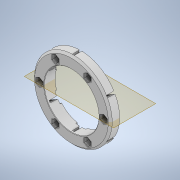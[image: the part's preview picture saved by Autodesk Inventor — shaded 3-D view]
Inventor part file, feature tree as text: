
AUTODESK INVENTOR PART (.ipt)
format: ipt  version: 2020 (Build 240168000, 168)  size: 5,638,656 bytes
history: native  units: in
note: dims shown in document units (in); Inventor stores cm internally (conversion verified against a paired STEP export)
features: extrude x7, sketch x7, other x4, chamfer x2, pattern_circular x2, reference x2, imported_body x1, boolean_combine x1, plane x1, fillet x1, projected_geometry x1
ambient origin geometry x8: Origin, YZ Plane, XZ Plane, XY Plane, X Axis, Y Axis, Z Axis, Center Point
bodies: Solid1 (feature_tree), Solid2 (feature_tree)
feature tree (29):
  extrude  "Extrusion1"  Depth=0.7in TaperAngle=0.0deg
  extrude  "Extrusion2"  Depth=2.3622in TaperAngle=360.0deg
  imported_body  "Base1"
  boolean_combine  "Combine1"
  extrude  "Extrusion3"  Depth=0.4375in
  extrude  "Extrusion4"  Depth=0.3in TaperAngle=0.0deg
  extrude  "Extrusion5"  Depth=0.0118in TaperAngle=0.0deg
  chamfer  "Chamfer1"  Distance=2.3622in Angle=360.0deg
  chamfer  "Chamfer2"  Distance=0.0118in
  plane  "Work Plane3"
  extrude  "Extrusion6"  Depth=0.025in TaperAngle=45.0deg
  pattern_circular  "Circular Pattern1"  [2 undecoded]
  extrude  "Extrusion7"  Depth=0.05in TaperAngle=0.0deg
  pattern_circular  "Circular Pattern2"  Count=6 Angle=360.0deg
  fillet  "Fillet1"  Radius=0.0118in
  sketch  "Sketch1"  dims[d0=3.5in d2=0.7in d3=0.0in]
  reference  "Reference1"
  sketch  "Sketch2"  dims[d4=0.2656in d5=2.3622in d7=360.0deg]
  reference  "Reference2"
  sketch  "Sketch3"  dims[d9=0.0in d10=0.0in d11=0.4375in]
  sketch  "Sketch4"  dims[d12=2.3622in d14=360.0deg d16=0.3in d17=0.0in]
  sketch  "Sketch5"  dims[d18=2.3622in d20=360.0deg d22=0.0118in d23=0.0in d24=2.3622in d26=360.0deg d28=0.0118in d29=0.0in]
  sketch  "Sketch7"  dims[d30=0.125in d31=0.125in d32=45.0deg d33=0.025in d34=0.125in d35=45.0deg]
  projected_geometry  "Projected Loop1"
  sketch  "Sketch9"  dims[d38=0.0079in d40=0.0079in d41=2.483in d42=0.0in d43=2.3622in d44=360.0deg d47=0.0118in d48=1.0in d49=0.0in d50=2.3622in d51=360.0deg d53=0.05in]
  other  "<userpath>\Documents\FRC\2020\Shooter\WheelAndFlywheelv3.iam"
  other  "WheelAndFlywheelv3.iam"
  other  "6 wheel Rev 4:1"
  other  "TopFlywheelClamp2:1"
note: 2 required parameter values undecoded (feature->parameter linkage not recoverable at this tier; creation-order binding heuristic only, values carry confidence <= 0.55)
